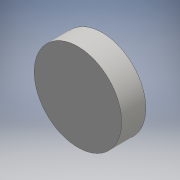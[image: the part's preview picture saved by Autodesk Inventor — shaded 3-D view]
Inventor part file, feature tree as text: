
AUTODESK INVENTOR PART (.ipt)
format: ipt  version: 2016 (Build 200138000, 138)  size: 86,528 bytes
history: native  units: mm
features: extrude x1, sketch x1
ambient origin geometry x8: Origin, YZ Plane, XZ Plane, XY Plane, X Axis, Y Axis, Z Axis, Center Point
bodies: Solid1 (feature_tree)
feature tree (2):
  extrude  "Extrusion1"  Depth=26.0mm TaperAngle=0.0deg
  sketch  "Sketch1"  dims[d0=94.0mm d1=26.0mm d2=0.0mm]
